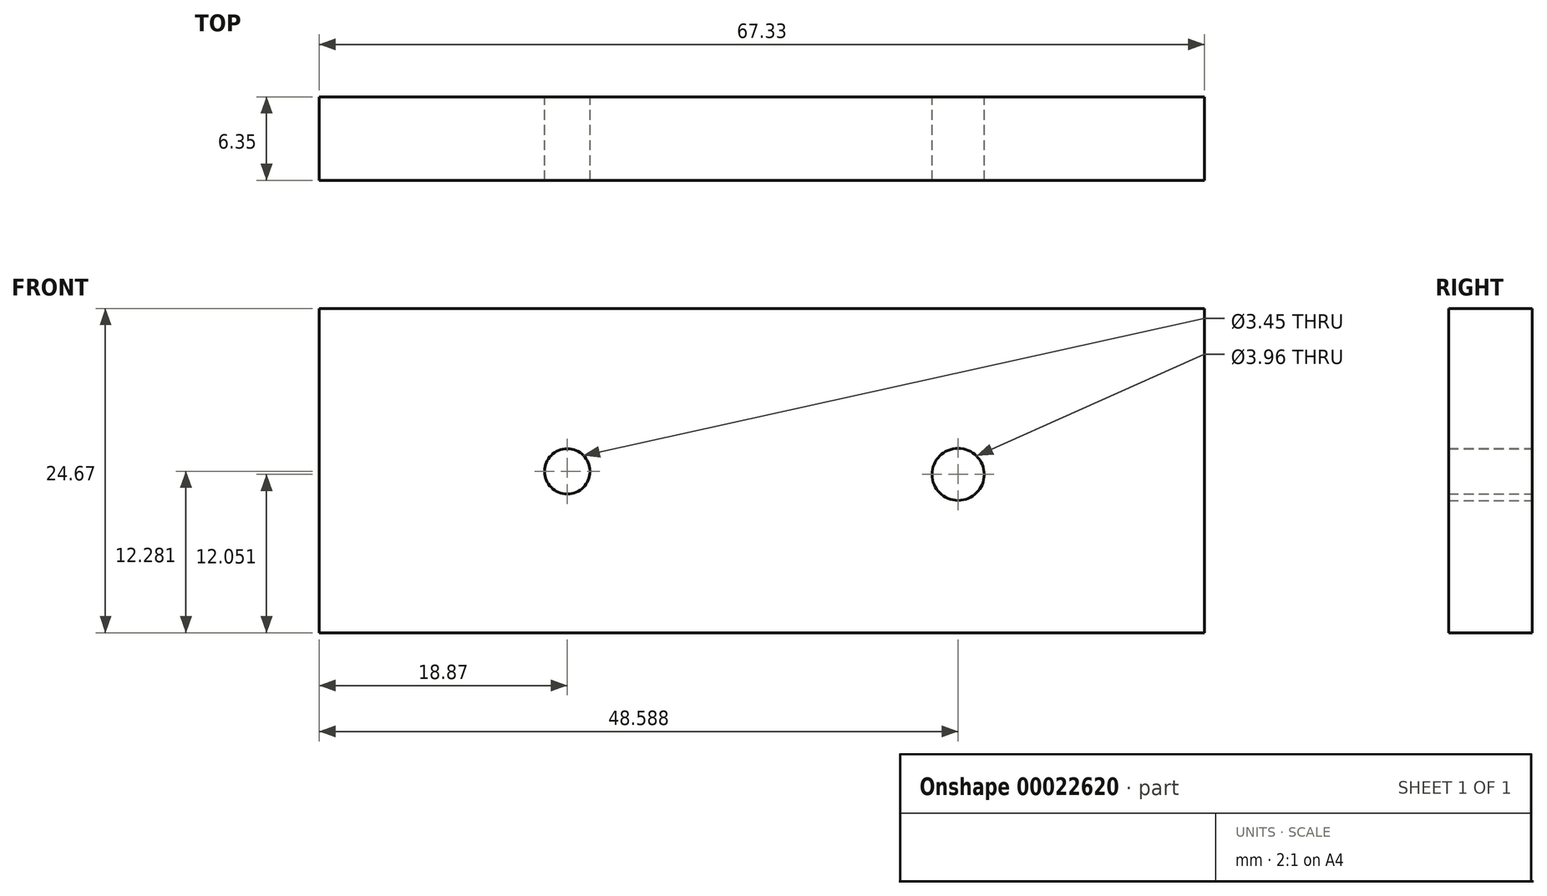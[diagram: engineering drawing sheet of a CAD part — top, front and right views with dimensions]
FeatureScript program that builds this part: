
annotation { "Feature Type Name" : "Feature", "Feature Type Description" : "" }
export const myFeature = defineFeature(function(context is Context, id is Id, definition is map)
    precondition{}
    {
        {
            var Q0;
            Q0=qCreatedBy(makeId("Front.planeOp"),FACE);
            var sketch = newSketch(context, id + "F0", { "sketchPlane" : qUnion([Q0])});
            skCircle(sketch, "E0", {"center": v(-24.62, 31.51) * mm, "radius": 1.73 * mm});
            skCircle(sketch, "E1", {"center": v(5.1, 31.28) * mm, "radius": 1.98 * mm});
            skPoint(sketch, "E2.rect.middle", {"position": v(-9.83, 31.56) * mm});
            skLineSegment(sketch, "E3.rect.bottom", {"start": v(-43.5, 43.9) * mm, "end": v(23.84, 43.9) * mm});
            skLineSegment(sketch, "E3.rect.top", {"start": v(-43.5, 19.23) * mm, "end": v(23.84, 19.23) * mm});
            skLineSegment(sketch, "E3.rect.left", {"start": v(-43.5, 43.9) * mm, "end": v(-43.5, 19.23) * mm});
            skLineSegment(sketch, "E3.rect.right", {"start": v(23.84, 43.9) * mm, "end": v(23.84, 19.23) * mm});
            skSolve(sketch);
        }
        {
            var Q0;
            Q0 = qSketchRegion(id + "F0", true);
            extrude(context, id + "F1", {"entities" : qUnion([Q0]), "depth" : 6.35 * mm});
        }
    });
